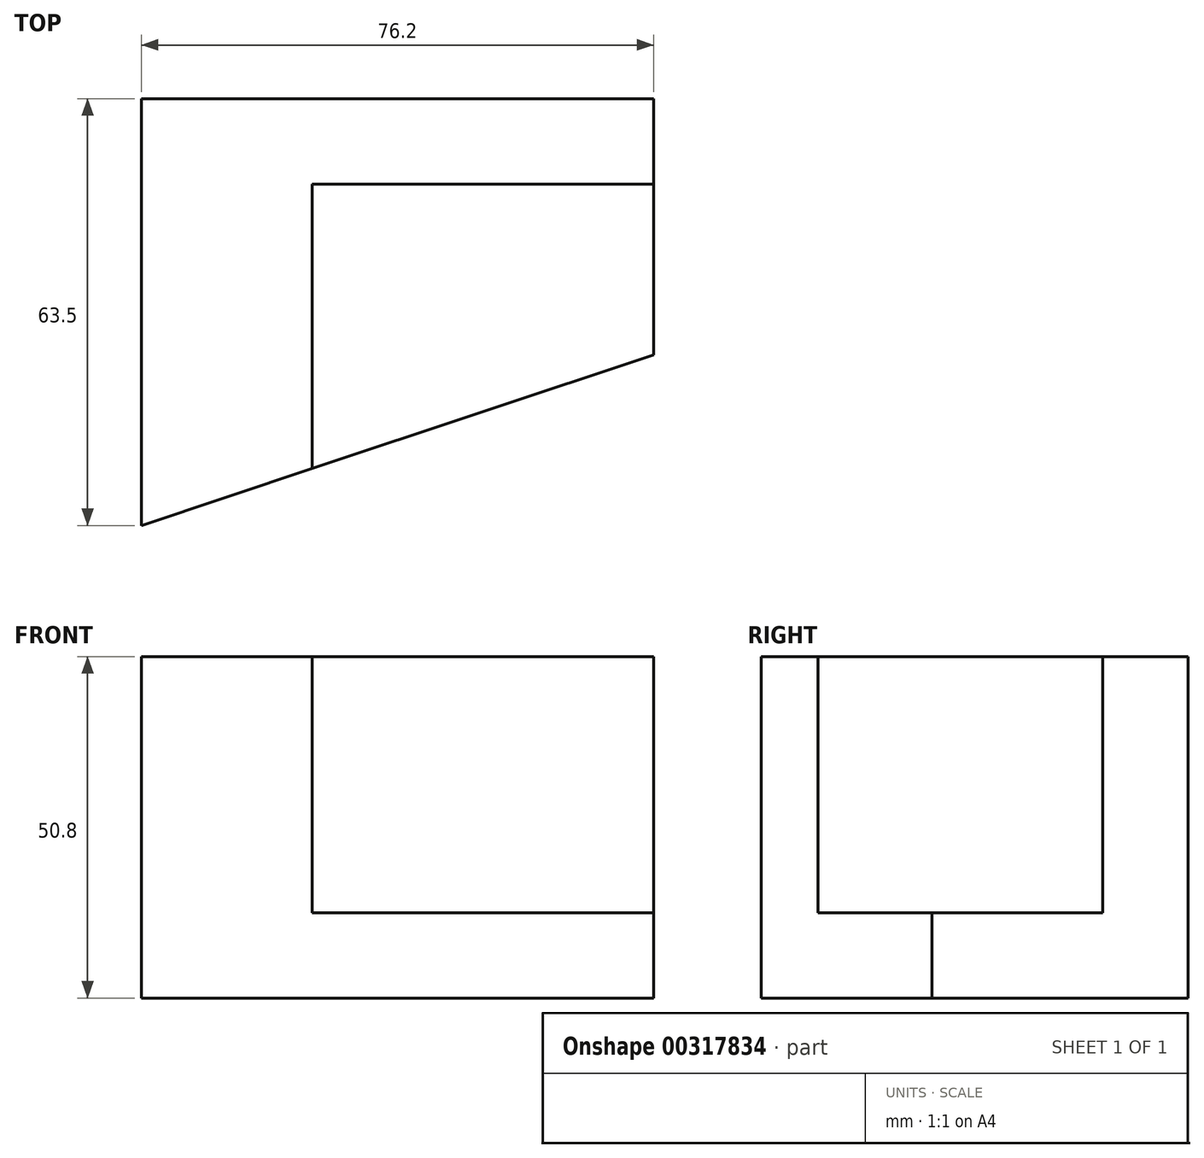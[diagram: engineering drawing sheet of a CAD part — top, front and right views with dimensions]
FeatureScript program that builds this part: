
annotation { "Feature Type Name" : "Feature", "Feature Type Description" : "" }
export const myFeature = defineFeature(function(context is Context, id is Id, definition is map)
    precondition{}
    {
        {
            var Q0;
            Q0=qCreatedBy(makeId("Top.planeOp"),FACE);
            var sketch = newSketch(context, id + "F0", { "sketchPlane" : qUnion([Q0])});
            skLineSegment(sketch, "E0.top", {"start": v(0, 63.5) * mm, "end": v(76.2, 63.5) * mm});
            skLineSegment(sketch, "E0.left", {"start": v(0, 0) * mm, "end": v(0, 63.5) * mm});
            skLineSegment(sketch, "E0.right", {"start": v(76.2, 25.4) * mm, "end": v(76.2, 63.5) * mm});
            skLineSegment(sketch, "E1", {"start": v(0, 0) * mm, "end": v(76.2, 25.4) * mm});
            skSolve(sketch);
        }
        {
            var Q0;
            Q0 = qSketchRegion(id + "F0", true);
            extrude(context, id + "F1", {"entities" : qUnion([Q0]), "depth" : 50.8 * mm});
        }
        {
            var Q0;
            Q0=qCreatedBy(makeId("Front.planeOp"),FACE);
            var sketch = newSketch(context, id + "F2", { "sketchPlane" : qUnion([Q0])});
            skLineSegment(sketch, "E2.bottom", {"start": v(25.4, 50.8) * mm, "end": v(76.2, 50.8) * mm});
            skLineSegment(sketch, "E2.top", {"start": v(25.4, 12.7) * mm, "end": v(76.2, 12.7) * mm});
            skLineSegment(sketch, "E2.left", {"start": v(25.4, 50.8) * mm, "end": v(25.4, 12.7) * mm});
            skLineSegment(sketch, "E2.right", {"start": v(76.2, 50.8) * mm, "end": v(76.2, 12.7) * mm});
            skSolve(sketch);
        }
        {
            var Q0;
            Q0 = qSketchRegion(id + "F2", true);
            extrude(context, id + "F3", {"entities" : qUnion([Q0]), "operationType" : NewBodyOperationType.REMOVE, "oppositeDirection" : true, "depth" : 50.8 * mm});
        }
    });
